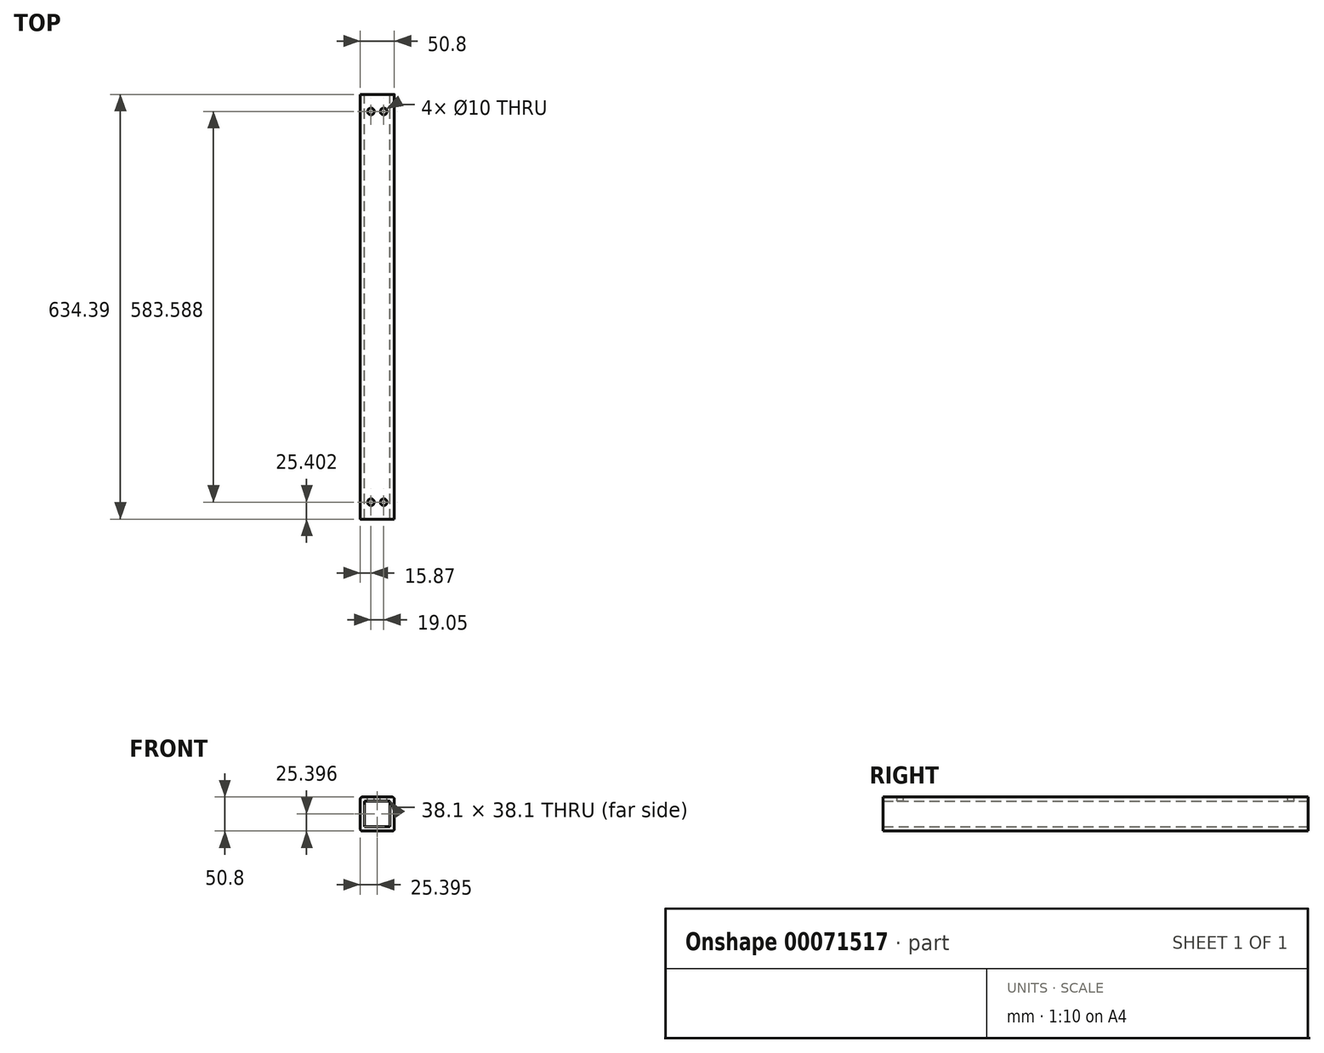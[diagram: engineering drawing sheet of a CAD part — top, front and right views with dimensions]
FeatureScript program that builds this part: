
annotation { "Feature Type Name" : "Feature", "Feature Type Description" : "" }
export const myFeature = defineFeature(function(context is Context, id is Id, definition is map)
    precondition{}
    {
        {
            var Q0;
            Q0=qCreatedBy(makeId("Front.planeOp"),FACE);
            var sketch = newSketch(context, id + "F0", { "sketchPlane" : qUnion([Q0])});
            skLineSegment(sketch, "E0.bottom", {"start": v(-28.47, 28.79) * mm, "end": v(15.98, 28.79) * mm});
            skLineSegment(sketch, "E0.top", {"start": v(-28.47, -22.01) * mm, "end": v(15.98, -22.01) * mm});
            skLineSegment(sketch, "E0.left", {"start": v(-31.64, 25.61) * mm, "end": v(-31.64, -18.84) * mm});
            skLineSegment(sketch, "E0.right", {"start": v(19.16, 25.61) * mm, "end": v(19.16, -18.84) * mm});
            skLineSegment(sketch, "E1.bottom", {"start": v(-25.3, 22.44) * mm, "end": v(12.8, 22.44) * mm});
            skLineSegment(sketch, "E1.top", {"start": v(-25.3, -15.66) * mm, "end": v(12.8, -15.66) * mm});
            skLineSegment(sketch, "E1.left", {"start": v(-25.3, 22.44) * mm, "end": v(-25.3, -15.66) * mm});
            skLineSegment(sketch, "E1.right", {"start": v(12.8, 22.44) * mm, "end": v(12.8, -15.66) * mm});
            skPoint(sketch, "E2.visualSharp", {"position": v(-31.64, 28.79) * mm});
            skArc(sketch, "E2.filletArc", {"start": v(-28.47, 28.79) * mm, "mid": v(-30.72, 27.86) * mm, "end": v(-31.64, 25.61) * mm});
            skPoint(sketch, "E3.visualSharp", {"position": v(-31.64, -22.01) * mm});
            skArc(sketch, "E3.filletArc", {"start": v(-31.64, -18.84) * mm, "mid": v(-30.72, -21.08) * mm, "end": v(-28.47, -22.01) * mm});
            skPoint(sketch, "E4.visualSharp", {"position": v(19.16, -22.01) * mm});
            skArc(sketch, "E4.filletArc", {"start": v(15.98, -22.01) * mm, "mid": v(18.23, -21.08) * mm, "end": v(19.16, -18.84) * mm});
            skPoint(sketch, "E5.visualSharp", {"position": v(19.16, 28.79) * mm});
            skArc(sketch, "E5.filletArc", {"start": v(19.16, 25.61) * mm, "mid": v(18.23, 27.86) * mm, "end": v(15.98, 28.79) * mm});
            skSolve(sketch);
        }
        {
            var Q0;
            Q0=qSketchRegion(id+"F0",true);
            extrude(context, id + "F1", {"entities" : qUnion([Q0]), "depth" : 634.4 * mm});
        }
        {
            var Q0;
            Q0=makeQuery(id+"F1.opExtrude","SWEPT_FACE",FACE,{"disambiguationData":[OSD([sQuery(id+"F0.wireOp",EDGE,"E0.bottom")])]});
            var sketch = newSketch(context, id + "F2", { "sketchPlane" : qUnion([Q0])});
            skCircle(sketch, "E6", {"center": v(-15.77, -25.4) * mm, "radius": 5 * mm});
            skCircle(sketch, "E7", {"center": v(3.28, -25.4) * mm, "radius": 5 * mm});
            skCircle(sketch, "E8", {"center": v(-15.77, -608.99) * mm, "radius": 5 * mm});
            skCircle(sketch, "E9", {"center": v(3.28, -608.99) * mm, "radius": 5 * mm});
            skSolve(sketch);
        }
        {
            var Q0;
            Q0=qSketchRegion(id+"F2",true);
            extrude(context, id + "F3", {"entities" : qUnion([Q0]), "operationType" : NewBodyOperationType.REMOVE, "oppositeDirection" : true, "depth" : 25.4 * mm});
        }
    });
